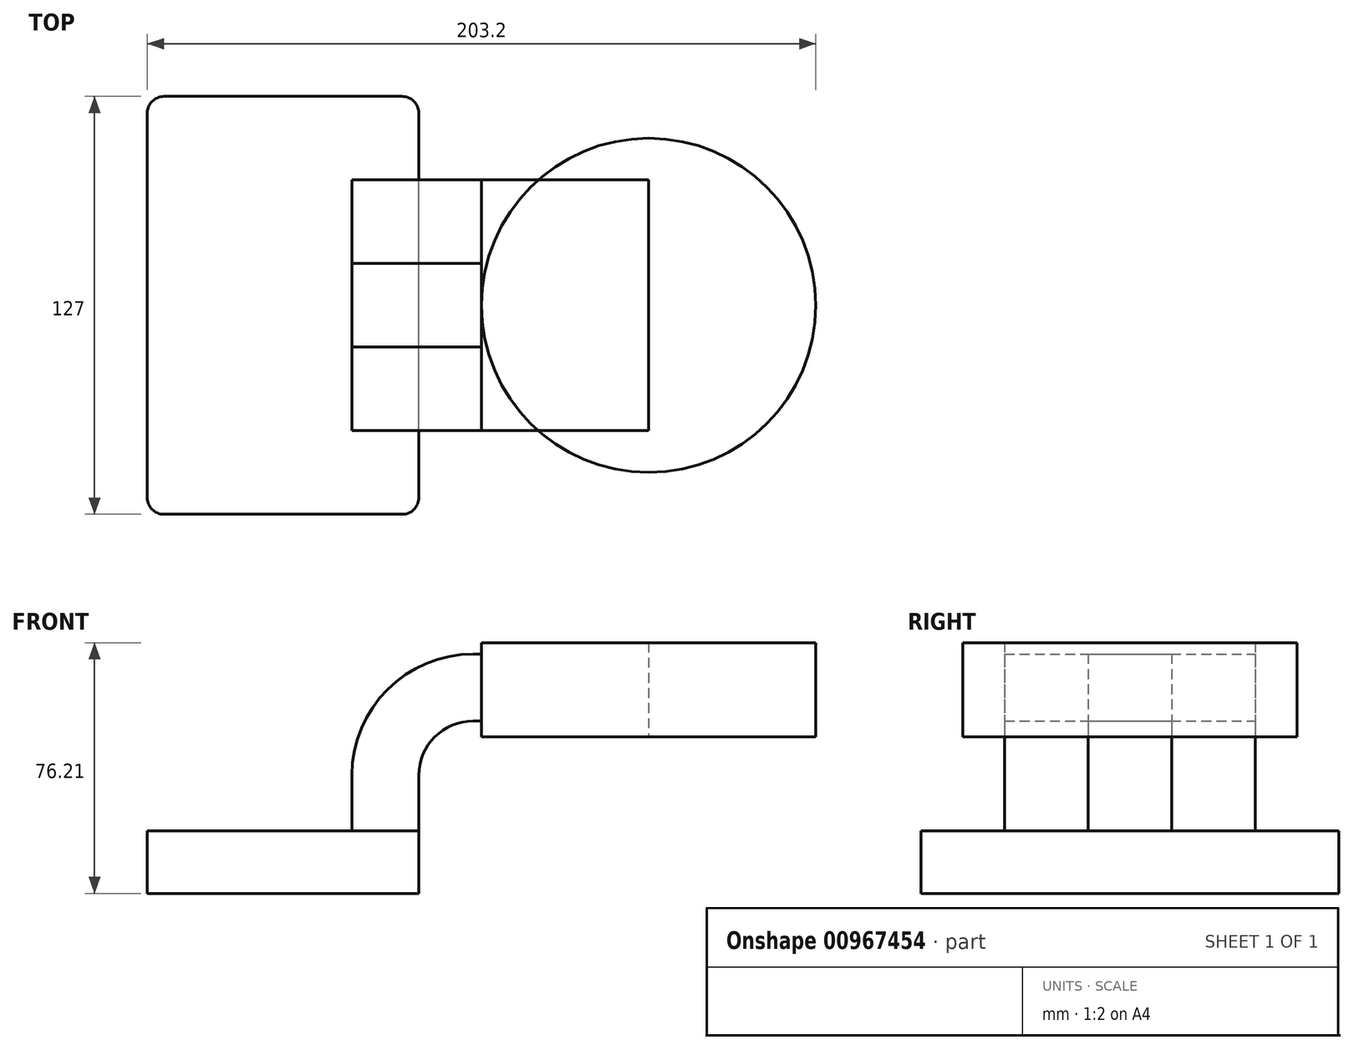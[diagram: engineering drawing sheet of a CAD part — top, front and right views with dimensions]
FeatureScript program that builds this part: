
annotation { "Feature Type Name" : "Feature", "Feature Type Description" : "" }
export const myFeature = defineFeature(function(context is Context, id is Id, definition is map)
    precondition{}
    {
        {
            var Q0;
            Q0=qCreatedBy(makeId("Front.planeOp"),FACE);
            var sketch = newSketch(context, id + "F0", { "sketchPlane" : qUnion([Q0])});
            skLineSegment(sketch, "E0.bottom", {"start": v(41.28, -9.52) * mm, "end": v(-41.27, -9.52) * mm});
            skLineSegment(sketch, "E0.top", {"start": v(41.27, 9.53) * mm, "end": v(-41.28, 9.53) * mm});
            skLineSegment(sketch, "E0.left", {"start": v(41.28, -9.52) * mm, "end": v(41.28, 9.53) * mm});
            skLineSegment(sketch, "E0.right", {"start": v(-41.27, -9.52) * mm, "end": v(-41.28, 9.53) * mm});
            skPoint(sketch, "E0.middle", {"position": v(0, 0) * mm});
            skLineSegment(sketch, "E1.bottom", {"start": v(111.13, 66.68) * mm, "end": v(60.33, 66.67) * mm});
            skLineSegment(sketch, "E1.top", {"start": v(111.13, 38.1) * mm, "end": v(60.33, 38.1) * mm});
            skLineSegment(sketch, "E1.left", {"start": v(111.13, 66.67) * mm, "end": v(111.13, 38.1) * mm});
            skLineSegment(sketch, "E1.right", {"start": v(60.33, 66.67) * mm, "end": v(60.33, 38.1) * mm});
            skPoint(sketch, "E1.middle", {"position": v(85.73, 52.39) * mm});
            skLineSegment(sketch, "E2", {"start": v(41.27, 9.53) * mm, "end": v(41.27, 26.37) * mm});
            skArc(sketch, "E3", {"start": v(41.27, 26.37) * mm, "mid": v(46.11, 38.04) * mm, "end": v(57.79, 42.88) * mm});
            skLineSegment(sketch, "E4", {"start": v(57.79, 42.88) * mm, "end": v(85.73, 42.88) * mm});
            skLineSegment(sketch, "E5.0", {"start": v(57.79, 63.23) * mm, "end": v(85.73, 63.23) * mm});
            skArc(sketch, "E5.1", {"start": v(20.92, 26.37) * mm, "mid": v(31.72, 52.43) * mm, "end": v(57.79, 63.23) * mm});
            skLineSegment(sketch, "E5.2", {"start": v(20.92, 9.53) * mm, "end": v(20.92, 26.37) * mm});
            skFitSpline(sketch, "E6", {"points": [v(-41.28, 9.53) * mm, v(57.78, 63.23) * mm], "startDerivative": vector(112.06, 42.24) * mm, "endDerivative": vector(139.28, -1.6) * mm});
            skSolve(sketch);
        }
        {
            var Q0;
            Q0=makeQuery(id+"F0.imprint","IMPRINT",FACE,{"disambiguationData":[TD([[makeQuery(id+"F0.imprint","IMPRINT",EDGE,{"derivedFrom":sQuery(id+"F0.wireOp",EDGE,"E5.1")}),1.0]])]});
            extrude(context, id + "F1", {"entities" : qUnion([Q0]), "endBound" : BoundingType.SYMMETRIC, "depth" : 25.4 * mm, "offsetDistance" : 25.4 * mm});
        }
        {
            var Q0;
            Q0=makeQuery(id+"F0.imprint","IMPRINT",FACE,{"disambiguationData":[TD([[makeQuery(id+"F0.imprint","IMPRINT",EDGE,{"derivedFrom":sQuery(id+"F0.wireOp",EDGE,"E0.bottom")}),-1.0]])]});
            extrude(context, id + "F2", {"entities" : qUnion([Q0]), "operationType" : NewBodyOperationType.ADD, "endBound" : BoundingType.SYMMETRIC, "depth" : 127 * mm, "offsetDistance" : 25.4 * mm});
        }
        {
            var Q0;
            {var subQ1=sQuery(id+"F0.wireOp",EDGE,"E1.bottom");Q0=makeQuery(id+"F0.imprint","IMPRINT",FACE,{"disambiguationData":[TD([[makeQuery(id+"F0.imprint","IMPRINT",EDGE,{"derivedFrom":subQ1}),1.0]])]});}
            extrude(context, id + "F3", {"entities" : qUnion([Q0]), "operationType" : NewBodyOperationType.ADD, "endBound" : BoundingType.SYMMETRIC, "depth" : 76.2 * mm, "offsetDistance" : 25.4 * mm});
        }
        {
            var Q0;
            {var subQ1=sQuery(id+"F0.wireOp",EDGE,"E2");Q0=makeQuery(id+"F0.imprint","IMPRINT",FACE,{"disambiguationData":[TD([[makeQuery(id+"F0.imprint","IMPRINT",EDGE,{"derivedFrom":subQ1}),1.0]])]});}
            extrude(context, id + "F4", {"entities" : qUnion([Q0]), "endBound" : BoundingType.SYMMETRIC, "depth" : 76.2 * mm, "offsetDistance" : 25.4 * mm});
        }
        {
            var Q0;
            {var subQ1=sQuery(id+"F0.wireOp",EDGE,"E1.bottom");Q0=makeQuery(id+"F0.imprint","IMPRINT",FACE,{"disambiguationData":[TD([[makeQuery(id+"F0.imprint","IMPRINT",EDGE,{"derivedFrom":subQ1}),1.0]])]});}
            var Q1;
            Q1=sQuery(id+"F0.wireOp",EDGE,"E1.left");
            revolve(context, id + "F5", {"surfaceOperationType" : NewSurfaceOperationType.NEW, "entities" : qUnion([Q0]), "axis" : qUnion([Q1]), "revolveType" : RevolveType.FULL});
        }
        {
            var Q0;
            Q0=makeQuery(id+"F2.opExtrude","CAP_EDGE",EDGE,{"disambiguationData":[OSD([sQuery(id+"F0.wireOp",EDGE,"E0.left")])],"isStart":false});
            var Q1;
            Q1=makeQuery(id+"F2.opExtrude","CAP_EDGE",EDGE,{"disambiguationData":[OSD([sQuery(id+"F0.wireOp",EDGE,"E0.right")])],"isStart":false});
            var Q2;
            Q2=makeQuery(id+"F2.opExtrude","CAP_EDGE",EDGE,{"disambiguationData":[OSD([sQuery(id+"F0.wireOp",EDGE,"E0.right")])],"isStart":true});
            var Q3;
            Q3=makeQuery(id+"F2.opExtrude","CAP_EDGE",EDGE,{"disambiguationData":[OSD([sQuery(id+"F0.wireOp",EDGE,"E0.left")])],"isStart":true});
            fillet(context, id + "F6", {"entities" : qUnion([Q0, Q1, Q2, Q3]), "radius" : 5.08 * mm, "tangentPropagation" : true, "allowEdgeOverflow" : false});
        }
    });
